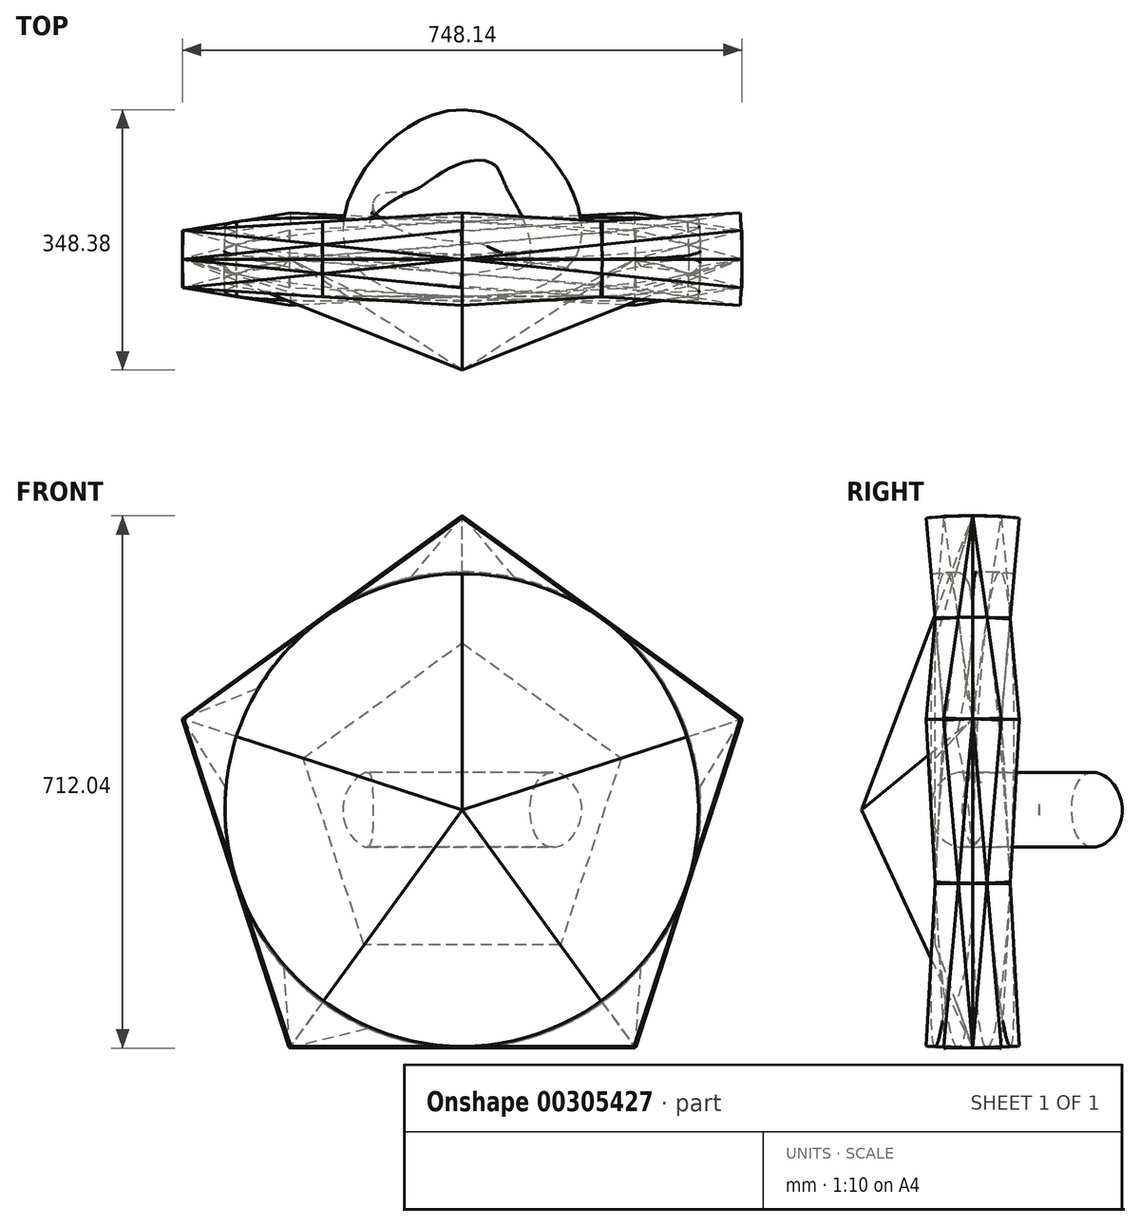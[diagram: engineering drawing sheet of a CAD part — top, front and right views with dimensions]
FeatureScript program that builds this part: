
annotation { "Feature Type Name" : "Feature", "Feature Type Description" : "" }
export const myFeature = defineFeature(function(context is Context, id is Id, definition is map)
    precondition{}
    {
        {
            var Q0;
            Q0=qCreatedBy(makeId("Front.planeOp"),FACE);
            var sketch = newSketch(context, id + "F0", { "sketchPlane" : qUnion([Q0])});
            skCircle(sketch, "E0", {"center": v(0, 0) * mm, "radius": 318.2 * mm});
            skCircle(sketch, "E1.cCircle", {"center": v(0, 0) * mm, "radius": 318.2 * mm, "construction": true});
            skLineSegment(sketch, "E1.0", {"start": v(374.07, 121.54) * mm, "end": v(231.19, -318.2) * mm});
            skLineSegment(sketch, "E1.1", {"start": v(231.19, -318.2) * mm, "end": v(-231.19, -318.2) * mm});
            skLineSegment(sketch, "E1.2", {"start": v(-231.19, -318.2) * mm, "end": v(-374.07, 121.54) * mm});
            skLineSegment(sketch, "E1.3", {"start": v(-374.07, 121.54) * mm, "end": v(0, 393.32) * mm});
            skLineSegment(sketch, "E1.4", {"start": v(0, 393.32) * mm, "end": v(374.07, 121.54) * mm});
            skPoint(sketch, "E1.0.midPoint", {"position": v(302.63, -98.33) * mm});
            skSolve(sketch);
        }
        {
            var Q0;
            {var subQ0=sQuery(id+"F0.wireOp",EDGE,"E0");var subQ4=makeQuery(id+"F0.imprint","INTERSECT",VERTEX,{"derivedFrom":[subQ0,sQuery(id+"F0.wireOp",EDGE,"E1.3")]});Q0=makeQuery(id+"F0.imprint","IMPRINT",FACE,{"disambiguationData":[TD([[makeQuery(id+"F0.imprint","IMPRINT",EDGE,{"disambiguationData":[TD([[subQ4,1.0]])],"derivedFrom":subQ0}),1.0]])]});}
            var Q1;
            {var subQ0=sQuery(id+"F0.wireOp",EDGE,"E1.3");var subQ1=sQuery(id+"F0.wireOp",EDGE,"E0");var subQ2=makeQuery(id+"F0.imprint","INTERSECT",VERTEX,{"derivedFrom":[subQ1,subQ0]});Q1=makeQuery(id+"F0.imprint","IMPRINT",FACE,{"disambiguationData":[TD([[makeQuery(id+"F0.imprint","IMPRINT",EDGE,{"disambiguationData":[TD([[subQ2,1.0]])],"derivedFrom":subQ1}),-1.0]])]});}
            var Q2;
            {var subQ0=sQuery(id+"F0.wireOp",EDGE,"E1.3");var subQ1=sQuery(id+"F0.wireOp",EDGE,"E0");var subQ2=makeQuery(id+"F0.imprint","INTERSECT",VERTEX,{"derivedFrom":[subQ1,subQ0]});Q2=makeQuery(id+"F0.imprint","IMPRINT",FACE,{"disambiguationData":[TD([[makeQuery(id+"F0.imprint","IMPRINT",EDGE,{"disambiguationData":[TD([[subQ2,-1.0]])],"derivedFrom":subQ1}),-1.0]])]});}
            var Q3;
            {var subQ0=sQuery(id+"F0.wireOp",EDGE,"E1.2");var subQ1=sQuery(id+"F0.wireOp",EDGE,"E0");var subQ2=makeQuery(id+"F0.imprint","INTERSECT",VERTEX,{"derivedFrom":[subQ1,subQ0]});Q3=makeQuery(id+"F0.imprint","IMPRINT",FACE,{"disambiguationData":[TD([[makeQuery(id+"F0.imprint","IMPRINT",EDGE,{"disambiguationData":[TD([[subQ2,-1.0]])],"derivedFrom":subQ1}),-1.0]])]});}
            var Q4;
            {var subQ0=sQuery(id+"F0.wireOp",EDGE,"E1.1");var subQ1=sQuery(id+"F0.wireOp",EDGE,"E0");var subQ2=makeQuery(id+"F0.imprint","INTERSECT",VERTEX,{"derivedFrom":[subQ1,subQ0]});Q4=makeQuery(id+"F0.imprint","IMPRINT",FACE,{"disambiguationData":[TD([[makeQuery(id+"F0.imprint","IMPRINT",EDGE,{"disambiguationData":[TD([[subQ2,-1.0]])],"derivedFrom":subQ1}),-1.0]])]});}
            var Q5;
            {var subQ0=sQuery(id+"F0.wireOp",EDGE,"E1.4");var subQ1=sQuery(id+"F0.wireOp",EDGE,"E0");var subQ2=makeQuery(id+"F0.imprint","INTERSECT",VERTEX,{"derivedFrom":[subQ1,subQ0]});Q5=makeQuery(id+"F0.imprint","IMPRINT",FACE,{"disambiguationData":[TD([[makeQuery(id+"F0.imprint","IMPRINT",EDGE,{"disambiguationData":[TD([[subQ2,1.0]])],"derivedFrom":subQ1}),-1.0]])]});}
            extrude(context, id + "F1", {"entities" : qUnion([Q0, Q1, Q2, Q3, Q4, Q5]), "depth" : 150 * mm, "hasDraft" : true, "draftAngle" : 65 * degree, "draftPullDirection" : true, "hasSecondDirectionDraft" : true, "secondDirectionDraftAngle" : 80 * degree, "secondDirectionDraftPullDirection" : true});
        }
        {
            var Q0;
            {var subQ0=sQuery(id+"F0.wireOp",EDGE,"E1.3");var subQ1=sQuery(id+"F0.wireOp",EDGE,"E0");var subQ2=makeQuery(id+"F0.imprint","INTERSECT",VERTEX,{"derivedFrom":[subQ1,subQ0]});Q0=makeQuery(id+"F0.imprint","IMPRINT",FACE,{"disambiguationData":[TD([[makeQuery(id+"F0.imprint","IMPRINT",EDGE,{"disambiguationData":[TD([[subQ2,1.0]])],"derivedFrom":subQ1}),-1.0]])]});}
            var Q1;
            {var subQ0=sQuery(id+"F0.wireOp",EDGE,"E1.3");var subQ1=sQuery(id+"F0.wireOp",EDGE,"E0");var subQ2=makeQuery(id+"F0.imprint","INTERSECT",VERTEX,{"derivedFrom":[subQ1,subQ0]});Q1=makeQuery(id+"F0.imprint","IMPRINT",FACE,{"disambiguationData":[TD([[makeQuery(id+"F0.imprint","IMPRINT",EDGE,{"disambiguationData":[TD([[subQ2,-1.0]])],"derivedFrom":subQ1}),-1.0]])]});}
            var Q2;
            {var subQ0=sQuery(id+"F0.wireOp",EDGE,"E1.2");var subQ1=sQuery(id+"F0.wireOp",EDGE,"E0");var subQ2=makeQuery(id+"F0.imprint","INTERSECT",VERTEX,{"derivedFrom":[subQ1,subQ0]});Q2=makeQuery(id+"F0.imprint","IMPRINT",FACE,{"disambiguationData":[TD([[makeQuery(id+"F0.imprint","IMPRINT",EDGE,{"disambiguationData":[TD([[subQ2,-1.0]])],"derivedFrom":subQ1}),-1.0]])]});}
            var Q3;
            {var subQ0=sQuery(id+"F0.wireOp",EDGE,"E1.1");var subQ1=sQuery(id+"F0.wireOp",EDGE,"E0");var subQ2=makeQuery(id+"F0.imprint","INTERSECT",VERTEX,{"derivedFrom":[subQ1,subQ0]});Q3=makeQuery(id+"F0.imprint","IMPRINT",FACE,{"disambiguationData":[TD([[makeQuery(id+"F0.imprint","IMPRINT",EDGE,{"disambiguationData":[TD([[subQ2,-1.0]])],"derivedFrom":subQ1}),-1.0]])]});}
            var Q4;
            {var subQ0=sQuery(id+"F0.wireOp",EDGE,"E1.4");var subQ1=sQuery(id+"F0.wireOp",EDGE,"E0");var subQ2=makeQuery(id+"F0.imprint","INTERSECT",VERTEX,{"derivedFrom":[subQ1,subQ0]});Q4=makeQuery(id+"F0.imprint","IMPRINT",FACE,{"disambiguationData":[TD([[makeQuery(id+"F0.imprint","IMPRINT",EDGE,{"disambiguationData":[TD([[subQ2,1.0]])],"derivedFrom":subQ1}),-1.0]])]});}
            var Q5;
            Q5=sQuery(id+"F0.wireOp",EDGE,"E1.2");
            revolve(context, id + "F2", {"entities" : qUnion([Q0, Q1, Q2, Q3, Q4]), "axis" : qUnion([Q5]), "revolveType" : RevolveType.SYMMETRIC, "angle" : 10 * degree});
        }
        {
            var Q0;
            {var subQ0=sQuery(id+"F0.wireOp",EDGE,"E1.3");var subQ1=sQuery(id+"F0.wireOp",EDGE,"E0");var subQ2=makeQuery(id+"F0.imprint","INTERSECT",VERTEX,{"derivedFrom":[subQ1,subQ0]});Q0=makeQuery(id+"F0.imprint","IMPRINT",FACE,{"disambiguationData":[TD([[makeQuery(id+"F0.imprint","IMPRINT",EDGE,{"disambiguationData":[TD([[subQ2,1.0]])],"derivedFrom":subQ1}),-1.0]])]});}
            var Q1;
            {var subQ0=sQuery(id+"F0.wireOp",EDGE,"E1.3");var subQ1=sQuery(id+"F0.wireOp",EDGE,"E0");var subQ2=makeQuery(id+"F0.imprint","INTERSECT",VERTEX,{"derivedFrom":[subQ1,subQ0]});Q1=makeQuery(id+"F0.imprint","IMPRINT",FACE,{"disambiguationData":[TD([[makeQuery(id+"F0.imprint","IMPRINT",EDGE,{"disambiguationData":[TD([[subQ2,-1.0]])],"derivedFrom":subQ1}),-1.0]])]});}
            var Q2;
            {var subQ0=sQuery(id+"F0.wireOp",EDGE,"E1.2");var subQ1=sQuery(id+"F0.wireOp",EDGE,"E0");var subQ2=makeQuery(id+"F0.imprint","INTERSECT",VERTEX,{"derivedFrom":[subQ1,subQ0]});Q2=makeQuery(id+"F0.imprint","IMPRINT",FACE,{"disambiguationData":[TD([[makeQuery(id+"F0.imprint","IMPRINT",EDGE,{"disambiguationData":[TD([[subQ2,-1.0]])],"derivedFrom":subQ1}),-1.0]])]});}
            var Q3;
            {var subQ0=sQuery(id+"F0.wireOp",EDGE,"E1.1");var subQ1=sQuery(id+"F0.wireOp",EDGE,"E0");var subQ2=makeQuery(id+"F0.imprint","INTERSECT",VERTEX,{"derivedFrom":[subQ1,subQ0]});Q3=makeQuery(id+"F0.imprint","IMPRINT",FACE,{"disambiguationData":[TD([[makeQuery(id+"F0.imprint","IMPRINT",EDGE,{"disambiguationData":[TD([[subQ2,-1.0]])],"derivedFrom":subQ1}),-1.0]])]});}
            var Q4;
            {var subQ0=sQuery(id+"F0.wireOp",EDGE,"E1.4");var subQ1=sQuery(id+"F0.wireOp",EDGE,"E0");var subQ2=makeQuery(id+"F0.imprint","INTERSECT",VERTEX,{"derivedFrom":[subQ1,subQ0]});Q4=makeQuery(id+"F0.imprint","IMPRINT",FACE,{"disambiguationData":[TD([[makeQuery(id+"F0.imprint","IMPRINT",EDGE,{"disambiguationData":[TD([[subQ2,1.0]])],"derivedFrom":subQ1}),-1.0]])]});}
            var Q5;
            Q5=sQuery(id+"F0.wireOp",EDGE,"E1.3");
            revolve(context, id + "F3", {"entities" : qUnion([Q0, Q1, Q2, Q3, Q4]), "axis" : qUnion([Q5]), "revolveType" : RevolveType.SYMMETRIC, "angle" : 10 * degree});
        }
        {
            var Q0;
            {var subQ0=sQuery(id+"F0.wireOp",EDGE,"E1.3");var subQ1=sQuery(id+"F0.wireOp",EDGE,"E0");var subQ2=makeQuery(id+"F0.imprint","INTERSECT",VERTEX,{"derivedFrom":[subQ1,subQ0]});Q0=makeQuery(id+"F0.imprint","IMPRINT",FACE,{"disambiguationData":[TD([[makeQuery(id+"F0.imprint","IMPRINT",EDGE,{"disambiguationData":[TD([[subQ2,1.0]])],"derivedFrom":subQ1}),-1.0]])]});}
            var Q1;
            {var subQ0=sQuery(id+"F0.wireOp",EDGE,"E1.3");var subQ1=sQuery(id+"F0.wireOp",EDGE,"E0");var subQ2=makeQuery(id+"F0.imprint","INTERSECT",VERTEX,{"derivedFrom":[subQ1,subQ0]});Q1=makeQuery(id+"F0.imprint","IMPRINT",FACE,{"disambiguationData":[TD([[makeQuery(id+"F0.imprint","IMPRINT",EDGE,{"disambiguationData":[TD([[subQ2,-1.0]])],"derivedFrom":subQ1}),-1.0]])]});}
            var Q2;
            {var subQ0=sQuery(id+"F0.wireOp",EDGE,"E1.2");var subQ1=sQuery(id+"F0.wireOp",EDGE,"E0");var subQ2=makeQuery(id+"F0.imprint","INTERSECT",VERTEX,{"derivedFrom":[subQ1,subQ0]});Q2=makeQuery(id+"F0.imprint","IMPRINT",FACE,{"disambiguationData":[TD([[makeQuery(id+"F0.imprint","IMPRINT",EDGE,{"disambiguationData":[TD([[subQ2,-1.0]])],"derivedFrom":subQ1}),-1.0]])]});}
            var Q3;
            {var subQ0=sQuery(id+"F0.wireOp",EDGE,"E1.1");var subQ1=sQuery(id+"F0.wireOp",EDGE,"E0");var subQ2=makeQuery(id+"F0.imprint","INTERSECT",VERTEX,{"derivedFrom":[subQ1,subQ0]});Q3=makeQuery(id+"F0.imprint","IMPRINT",FACE,{"disambiguationData":[TD([[makeQuery(id+"F0.imprint","IMPRINT",EDGE,{"disambiguationData":[TD([[subQ2,-1.0]])],"derivedFrom":subQ1}),-1.0]])]});}
            var Q4;
            {var subQ0=sQuery(id+"F0.wireOp",EDGE,"E1.4");var subQ1=sQuery(id+"F0.wireOp",EDGE,"E0");var subQ2=makeQuery(id+"F0.imprint","INTERSECT",VERTEX,{"derivedFrom":[subQ1,subQ0]});Q4=makeQuery(id+"F0.imprint","IMPRINT",FACE,{"disambiguationData":[TD([[makeQuery(id+"F0.imprint","IMPRINT",EDGE,{"disambiguationData":[TD([[subQ2,1.0]])],"derivedFrom":subQ1}),-1.0]])]});}
            var Q5;
            Q5=sQuery(id+"F0.wireOp",EDGE,"E1.1");
            revolve(context, id + "F4", {"entities" : qUnion([Q0, Q1, Q2, Q3, Q4]), "axis" : qUnion([Q5]), "revolveType" : RevolveType.SYMMETRIC, "angle" : 10 * degree});
        }
        {
            var Q0;
            {var subQ0=sQuery(id+"F0.wireOp",EDGE,"E1.4");var subQ1=sQuery(id+"F0.wireOp",EDGE,"E0");var subQ2=makeQuery(id+"F0.imprint","INTERSECT",VERTEX,{"derivedFrom":[subQ1,subQ0]});Q0=makeQuery(id+"F0.imprint","IMPRINT",FACE,{"disambiguationData":[TD([[makeQuery(id+"F0.imprint","IMPRINT",EDGE,{"disambiguationData":[TD([[subQ2,1.0]])],"derivedFrom":subQ1}),-1.0]])]});}
            var Q1;
            {var subQ0=sQuery(id+"F0.wireOp",EDGE,"E1.1");var subQ1=sQuery(id+"F0.wireOp",EDGE,"E0");var subQ2=makeQuery(id+"F0.imprint","INTERSECT",VERTEX,{"derivedFrom":[subQ1,subQ0]});Q1=makeQuery(id+"F0.imprint","IMPRINT",FACE,{"disambiguationData":[TD([[makeQuery(id+"F0.imprint","IMPRINT",EDGE,{"disambiguationData":[TD([[subQ2,-1.0]])],"derivedFrom":subQ1}),-1.0]])]});}
            var Q2;
            {var subQ0=sQuery(id+"F0.wireOp",EDGE,"E1.3");var subQ1=sQuery(id+"F0.wireOp",EDGE,"E0");var subQ2=makeQuery(id+"F0.imprint","INTERSECT",VERTEX,{"derivedFrom":[subQ1,subQ0]});Q2=makeQuery(id+"F0.imprint","IMPRINT",FACE,{"disambiguationData":[TD([[makeQuery(id+"F0.imprint","IMPRINT",EDGE,{"disambiguationData":[TD([[subQ2,1.0]])],"derivedFrom":subQ1}),-1.0]])]});}
            var Q3;
            {var subQ0=sQuery(id+"F0.wireOp",EDGE,"E1.3");var subQ1=sQuery(id+"F0.wireOp",EDGE,"E0");var subQ2=makeQuery(id+"F0.imprint","INTERSECT",VERTEX,{"derivedFrom":[subQ1,subQ0]});Q3=makeQuery(id+"F0.imprint","IMPRINT",FACE,{"disambiguationData":[TD([[makeQuery(id+"F0.imprint","IMPRINT",EDGE,{"disambiguationData":[TD([[subQ2,-1.0]])],"derivedFrom":subQ1}),-1.0]])]});}
            var Q4;
            {var subQ0=sQuery(id+"F0.wireOp",EDGE,"E1.2");var subQ1=sQuery(id+"F0.wireOp",EDGE,"E0");var subQ2=makeQuery(id+"F0.imprint","INTERSECT",VERTEX,{"derivedFrom":[subQ1,subQ0]});Q4=makeQuery(id+"F0.imprint","IMPRINT",FACE,{"disambiguationData":[TD([[makeQuery(id+"F0.imprint","IMPRINT",EDGE,{"disambiguationData":[TD([[subQ2,-1.0]])],"derivedFrom":subQ1}),-1.0]])]});}
            var Q5;
            Q5=sQuery(id+"F0.wireOp",EDGE,"E1.4");
            revolve(context, id + "F5", {"entities" : qUnion([Q0, Q1, Q2, Q3, Q4]), "axis" : qUnion([Q5]), "revolveType" : RevolveType.SYMMETRIC, "angle" : 10 * degree});
        }
        {
            var Q0;
            {var subQ0=sQuery(id+"F0.wireOp",EDGE,"E1.3");var subQ1=sQuery(id+"F0.wireOp",EDGE,"E0");var subQ2=makeQuery(id+"F0.imprint","INTERSECT",VERTEX,{"derivedFrom":[subQ1,subQ0]});Q0=makeQuery(id+"F0.imprint","IMPRINT",FACE,{"disambiguationData":[TD([[makeQuery(id+"F0.imprint","IMPRINT",EDGE,{"disambiguationData":[TD([[subQ2,-1.0]])],"derivedFrom":subQ1}),-1.0]])]});}
            var Q1;
            {var subQ0=sQuery(id+"F0.wireOp",EDGE,"E1.3");var subQ1=sQuery(id+"F0.wireOp",EDGE,"E0");var subQ2=makeQuery(id+"F0.imprint","INTERSECT",VERTEX,{"derivedFrom":[subQ1,subQ0]});Q1=makeQuery(id+"F0.imprint","IMPRINT",FACE,{"disambiguationData":[TD([[makeQuery(id+"F0.imprint","IMPRINT",EDGE,{"disambiguationData":[TD([[subQ2,1.0]])],"derivedFrom":subQ1}),-1.0]])]});}
            var Q2;
            {var subQ0=sQuery(id+"F0.wireOp",EDGE,"E1.2");var subQ1=sQuery(id+"F0.wireOp",EDGE,"E0");var subQ2=makeQuery(id+"F0.imprint","INTERSECT",VERTEX,{"derivedFrom":[subQ1,subQ0]});Q2=makeQuery(id+"F0.imprint","IMPRINT",FACE,{"disambiguationData":[TD([[makeQuery(id+"F0.imprint","IMPRINT",EDGE,{"disambiguationData":[TD([[subQ2,-1.0]])],"derivedFrom":subQ1}),-1.0]])]});}
            var Q3;
            {var subQ0=sQuery(id+"F0.wireOp",EDGE,"E1.1");var subQ1=sQuery(id+"F0.wireOp",EDGE,"E0");var subQ2=makeQuery(id+"F0.imprint","INTERSECT",VERTEX,{"derivedFrom":[subQ1,subQ0]});Q3=makeQuery(id+"F0.imprint","IMPRINT",FACE,{"disambiguationData":[TD([[makeQuery(id+"F0.imprint","IMPRINT",EDGE,{"disambiguationData":[TD([[subQ2,-1.0]])],"derivedFrom":subQ1}),-1.0]])]});}
            var Q4;
            {var subQ0=sQuery(id+"F0.wireOp",EDGE,"E1.4");var subQ1=sQuery(id+"F0.wireOp",EDGE,"E0");var subQ2=makeQuery(id+"F0.imprint","INTERSECT",VERTEX,{"derivedFrom":[subQ1,subQ0]});Q4=makeQuery(id+"F0.imprint","IMPRINT",FACE,{"disambiguationData":[TD([[makeQuery(id+"F0.imprint","IMPRINT",EDGE,{"disambiguationData":[TD([[subQ2,1.0]])],"derivedFrom":subQ1}),-1.0]])]});}
            var Q5;
            Q5=sQuery(id+"F0.wireOp",EDGE,"E1.1");
            revolve(context, id + "F6", {"entities" : qUnion([Q0, Q1, Q2, Q3, Q4]), "axis" : qUnion([Q5]), "revolveType" : RevolveType.SYMMETRIC, "angle" : 10 * degree});
        }
        {
            var Q0;
            Q0=qCreatedBy(makeId("Front.planeOp"),FACE);
            var sketch = newSketch(context, id + "F7", { "sketchPlane" : qUnion([Q0])});
            skLineSegment(sketch, "E2", {"start": v(0, 0) * mm, "end": v(100, 0) * mm, "construction": true});
            skCircle(sketch, "E3", {"center": v(100, 0) * mm, "radius": 50 * mm});
            skSolve(sketch);
        }
        {
            var Q0;
            Q0=qCreatedBy(makeId("Top.planeOp"),FACE);
            var sketch = newSketch(context, id + "F8", { "sketchPlane" : qUnion([Q0])});
            skLineSegment(sketch, "E4", {"start": v(0, 0) * mm, "end": v(-150, 0) * mm, "construction": true});
            skLineSegment(sketch, "E5", {"start": v(0, 0) * mm, "end": v(150, 0) * mm, "construction": true});
            skLineSegment(sketch, "E6", {"start": v(0, 0) * mm, "end": v(0, 200) * mm, "construction": true});
            skFitSpline(sketch, "E7", {"points": [v(150, 0) * mm, v(0, 200) * mm, v(-150, 0) * mm, v(150, 0) * mm]});
            skSolve(sketch);
        }
        {
            var Q0;
            Q0=makeQuery(id+"F1.opExtrude","CAP_FACE",FACE,{"disambiguationData":[OSD([sQuery(id+"F0.wireOp",EDGE,"E1.0"),sQuery(id+"F0.wireOp",EDGE,"E1.1"),sQuery(id+"F0.wireOp",EDGE,"E1.2"),sQuery(id+"F0.wireOp",EDGE,"E1.3"),sQuery(id+"F0.wireOp",EDGE,"E1.4")])],"isStart":true});
            extrude(context, id + "F9", {"entities" : qUnion([Q0]), "operationType" : NewBodyOperationType.REMOVE, "oppositeDirection" : true, "depth" : 50 * mm, "hasDraft" : true, "draftAngle" : 70 * degree, "draftPullDirection" : true});
        }
        {
            var Q0;
            Q0=makeQuery(id+"F7.imprint","IMPRINT",FACE,{"disambiguationData":[TD([[makeQuery(id+"F7.imprint","IMPRINT",EDGE,{"derivedFrom":sQuery(id+"F7.wireOp",EDGE,"E3")}),1.0]])]});
            var Q1;
            Q1=sQuery(id+"F8.wireOp",EDGE,"E7");
            sweep(context, id + "F10", {"profiles" : qUnion([Q0]), "path" : qUnion([Q1])});
        }
    });
